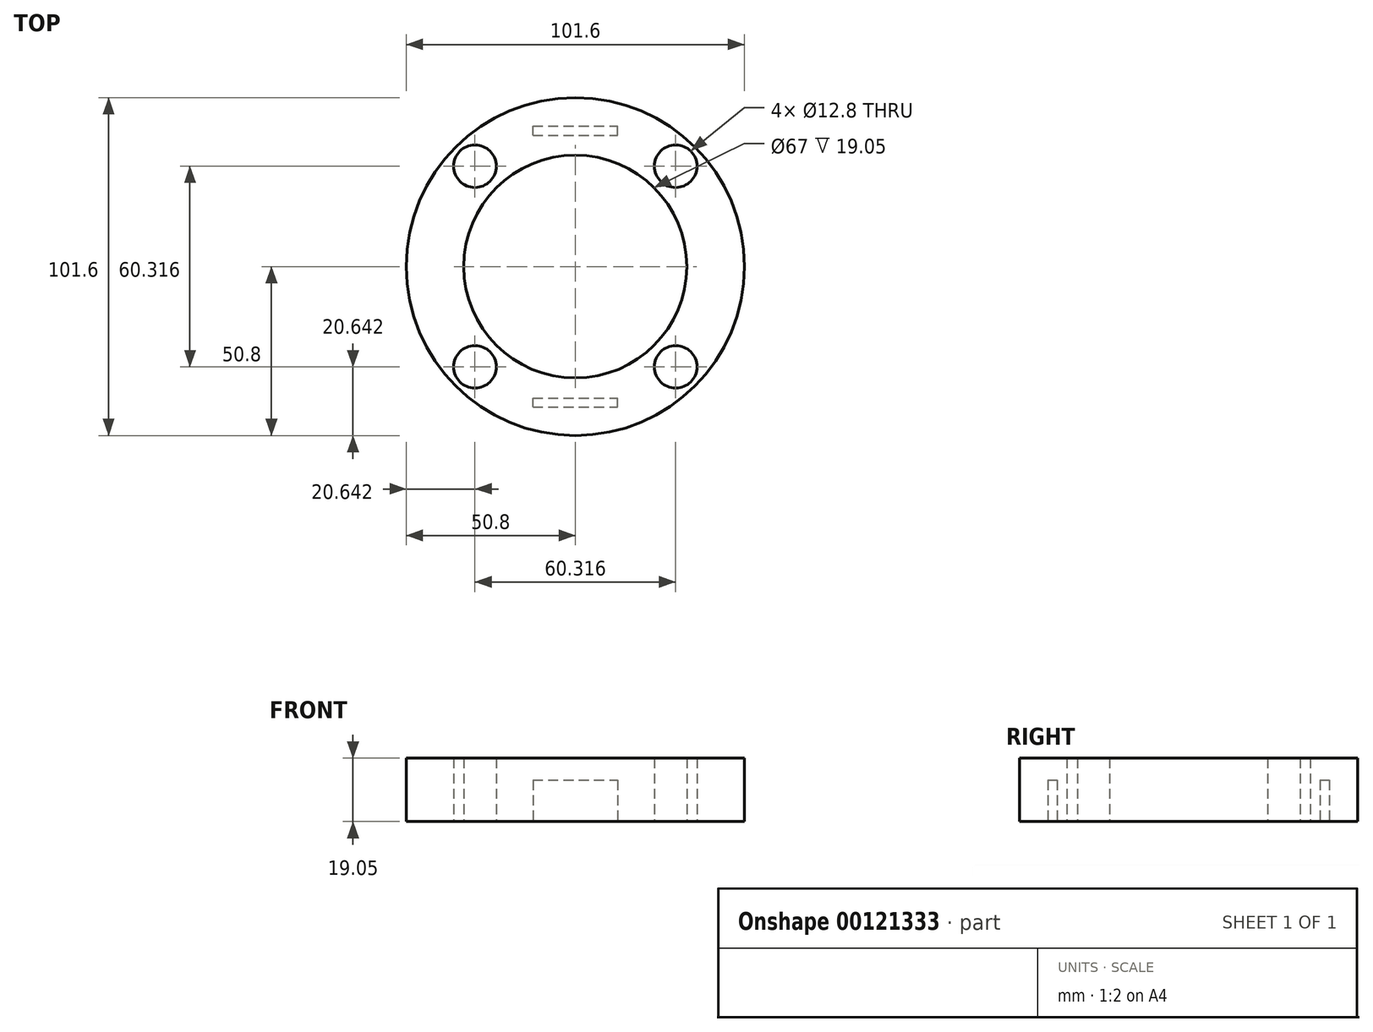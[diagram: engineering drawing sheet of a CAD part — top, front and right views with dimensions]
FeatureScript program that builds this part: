
annotation { "Feature Type Name" : "Feature", "Feature Type Description" : "" }
export const myFeature = defineFeature(function(context is Context, id is Id, definition is map)
    precondition{}
    {
        {
            var Q0;
            Q0=qCreatedBy(makeId("Top.planeOp"),FACE);
            var sketch = newSketch(context, id + "F0", { "sketchPlane" : qUnion([Q0])});
            skCircle(sketch, "E0", {"center": v(0, 0) * mm, "radius": 50.8 * mm});
            skCircle(sketch, "E1", {"center": v(0, 0) * mm, "radius": 33.5 * mm});
            skLineSegment(sketch, "E2", {"start": v(0, 50.8) * mm, "end": v(0, 33.5) * mm, "construction": true});
            skLineSegment(sketch, "E3", {"start": v(-35.92, 35.92) * mm, "end": v(35.92, -35.92) * mm, "construction": true});
            skLineSegment(sketch, "E4", {"start": v(-35.92, -35.92) * mm, "end": v(35.92, 35.92) * mm, "construction": true});
            skCircle(sketch, "E5", {"center": v(30.16, -30.16) * mm, "radius": 6.4 * mm});
            skCircle(sketch, "E6.1.0", {"center": v(30.16, 30.16) * mm, "radius": 6.4 * mm});
            skCircle(sketch, "E6.2.0", {"center": v(-30.16, 30.16) * mm, "radius": 6.4 * mm});
            skCircle(sketch, "E6.3.0", {"center": v(-30.16, -30.16) * mm, "radius": 6.4 * mm});
            skSolve(sketch);
        }
        {
            var Q0;
            Q0 = qSketchRegion(id + "F0", true);
            extrude(context, id + "F1", {"entities" : qUnion([Q0]), "depth" : 19.05 * mm});
        }
        {
            var Q0;
            Q0=makeQuery(id+"F1.opExtrude","CAP_FACE",FACE,{"disambiguationData":[OSD([sQuery(id+"F0.wireOp",EDGE,"E0"),sQuery(id+"F0.wireOp",EDGE,"E1"),sQuery(id+"F0.wireOp",EDGE,"E5"),sQuery(id+"F0.wireOp",EDGE,"E6.1.0"),sQuery(id+"F0.wireOp",EDGE,"E6.2.0"),sQuery(id+"F0.wireOp",EDGE,"E6.3.0")])],"isStart":true});
            var sketch = newSketch(context, id + "F2", { "sketchPlane" : qUnion([Q0])});
            skLineSegment(sketch, "E7.bottom", {"start": v(-12.75, -39.5) * mm, "end": v(12.75, -39.5) * mm});
            skLineSegment(sketch, "E7.top", {"start": v(-12.75, -42.27) * mm, "end": v(12.75, -42.27) * mm});
            skLineSegment(sketch, "E7.left", {"start": v(-12.75, -39.5) * mm, "end": v(-12.75, -42.27) * mm});
            skLineSegment(sketch, "E7.right", {"start": v(12.75, -39.5) * mm, "end": v(12.75, -42.27) * mm});
            skLineSegment(sketch, "E8", {"start": v(-33.5, 0) * mm, "end": v(-50.8, 0) * mm, "construction": true});
            skLineSegment(sketch, "E9.bottom", {"start": v(-12.75, 42.27) * mm, "end": v(12.75, 42.27) * mm});
            skLineSegment(sketch, "E9.top", {"start": v(-12.75, 39.5) * mm, "end": v(12.75, 39.5) * mm});
            skLineSegment(sketch, "E9.left", {"start": v(-12.75, 42.27) * mm, "end": v(-12.75, 39.5) * mm});
            skLineSegment(sketch, "E9.right", {"start": v(12.75, 42.27) * mm, "end": v(12.75, 39.5) * mm});
            skSolve(sketch);
        }
        {
            var Q0;
            Q0 = qSketchRegion(id + "F2", true);
            extrude(context, id + "F3", {"entities" : qUnion([Q0]), "operationType" : NewBodyOperationType.REMOVE, "oppositeDirection" : true, "depth" : 12.5 * mm});
        }
    });
